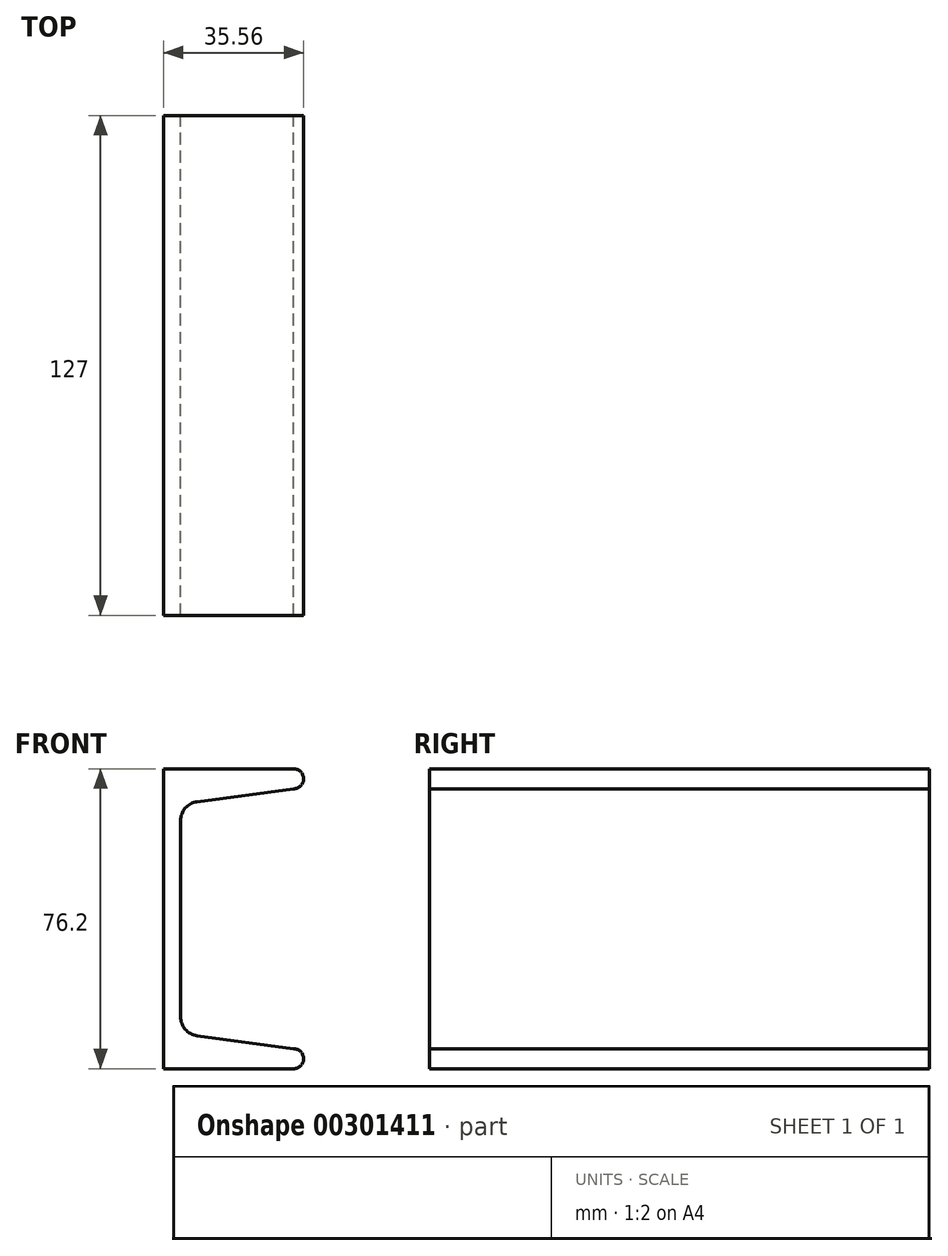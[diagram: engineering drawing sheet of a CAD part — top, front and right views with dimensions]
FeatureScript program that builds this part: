
annotation { "Feature Type Name" : "Feature", "Feature Type Description" : "" }
export const myFeature = defineFeature(function(context is Context, id is Id, definition is map)
    precondition{}
    {
        {
            var Q0;
            Q0=qCreatedBy(makeId("Front.planeOp"),FACE);
            var sketch = newSketch(context, id + "F0", { "sketchPlane" : qUnion([Q0])});
            skLineSegment(sketch, "E0", {"start": v(0, 0) * mm, "end": v(0, -38.1) * mm});
            skLineSegment(sketch, "E1", {"start": v(0, -38.1) * mm, "end": v(33.02, -38.1) * mm});
            skArc(sketch, "E2", {"start": v(33.02, -38.1) * mm, "mid": v(35.56, -35.56) * mm, "end": v(33.02, -33.02) * mm});
            skLineSegment(sketch, "E3", {"start": v(33.02, -33.02) * mm, "end": v(8.52, -29.72) * mm});
            skLineSegment(sketch, "E4", {"start": v(4.32, -24.91) * mm, "end": v(4.32, 0) * mm});
            skPoint(sketch, "E5.visualSharp", {"position": v(4.32, -29.16) * mm});
            skArc(sketch, "E5.filletArc", {"start": v(4.32, -24.91) * mm, "mid": v(5.52, -28.1) * mm, "end": v(8.52, -29.72) * mm});
            skLineSegment(sketch, "E6", {"start": v(0, -38.1) * mm, "end": v(58.4, -38.1) * mm, "construction": true});
            skArc(sketch, "E7.MirrorCS", {"start": v(4.32, 24.91) * mm, "mid": v(5.52, 28.1) * mm, "end": v(8.52, 29.72) * mm});
            skLineSegment(sketch, "E8.MirrorCS", {"start": v(0, 38.1) * mm, "end": v(33.02, 38.1) * mm});
            skLineSegment(sketch, "E9.MirrorCS", {"start": v(4.32, 24.91) * mm, "end": v(4.32, 0) * mm});
            skLineSegment(sketch, "E10.MirrorCS", {"start": v(0, 0) * mm, "end": v(0, 38.1) * mm});
            skLineSegment(sketch, "E11.MirrorCS", {"start": v(33.02, 33.02) * mm, "end": v(8.52, 29.72) * mm});
            skArc(sketch, "E12.MirrorCS", {"start": v(33.02, 38.1) * mm, "mid": v(35.56, 35.56) * mm, "end": v(33.02, 33.02) * mm});
            skPoint(sketch, "E13.MirrorP", {"position": v(4.32, 29.16) * mm});
            skSolve(sketch);
        }
        {
            var Q0;
            Q0 = qSketchRegion(id + "F0", true);
            extrude(context, id + "F1", {"entities" : qUnion([Q0]), "depth" : 127 * mm});
        }
    });
